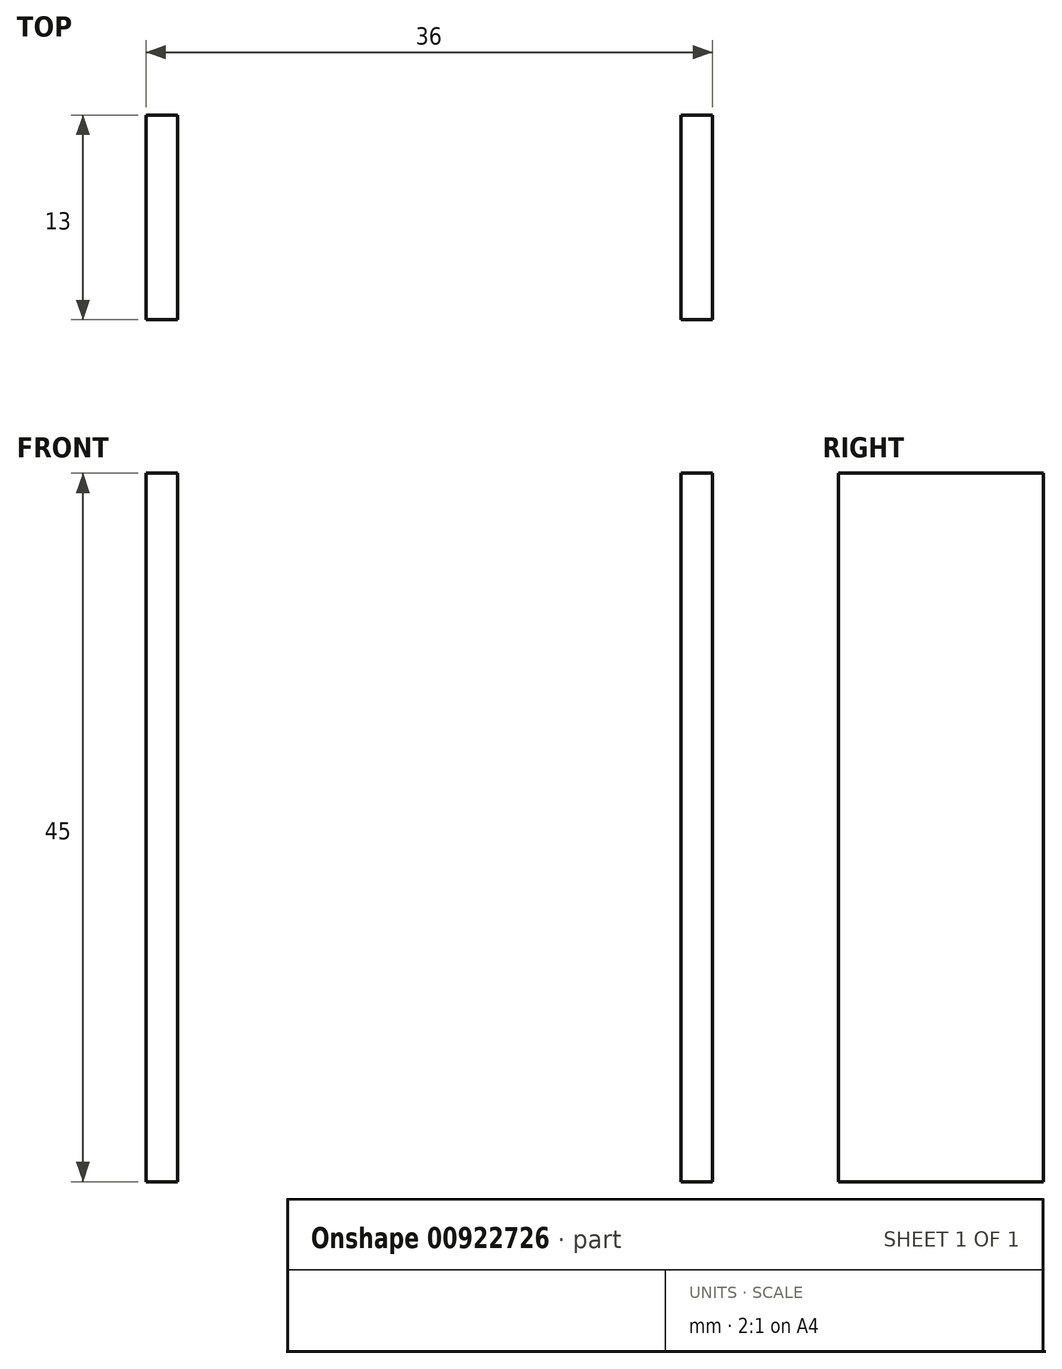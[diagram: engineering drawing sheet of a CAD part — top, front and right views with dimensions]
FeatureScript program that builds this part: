
annotation { "Feature Type Name" : "Feature", "Feature Type Description" : "" }
export const myFeature = defineFeature(function(context is Context, id is Id, definition is map)
    precondition{}
    {
        {
            var Q0;
            Q0=qCreatedBy(makeId("Right.planeOp"),FACE);
            var sketch = newSketch(context, id + "F0", { "sketchPlane" : qUnion([Q0])});
            skLineSegment(sketch, "E0.bottom", {"start": v(6.5, -22.5) * mm, "end": v(-6.5, -22.5) * mm});
            skLineSegment(sketch, "E0.top", {"start": v(6.5, 22.5) * mm, "end": v(-6.5, 22.5) * mm});
            skLineSegment(sketch, "E0.left", {"start": v(6.5, -22.5) * mm, "end": v(6.5, 22.5) * mm});
            skLineSegment(sketch, "E0.right", {"start": v(-6.5, -22.5) * mm, "end": v(-6.5, 22.5) * mm});
            skPoint(sketch, "E0.middle", {"position": v(0, 0) * mm});
            skSolve(sketch);
        }
        {
            var Q0;
            Q0 = qSketchRegion(id + "F0", true);
            extrude(context, id + "F1", {"entities" : qUnion([Q0]), "endBound" : BoundingType.SYMMETRIC, "depth" : 2 * mm, "offsetDistance" : 25 * mm});
        }
        {
            var Q0;
            Q0=makeQuery(id+"F1.opExtrude","SWEPT_BODY",BODY,{"disambiguationData":[OSD([sQuery(id+"F0.wireOp",EDGE,"E0.bottom"),sQuery(id+"F0.wireOp",EDGE,"E0.top"),sQuery(id+"F0.wireOp",EDGE,"E0.left"),sQuery(id+"F0.wireOp",EDGE,"E0.right")])]});
            transform(context, id + "F2", {"entities" : qUnion([Q0]), "transformType" : TransformType.TRANSLATION_3D, "dx" : -34 * mm, "dy" : 0 * mm, "dz" : 0 * mm, "makeCopy" : true});
        }
    });
